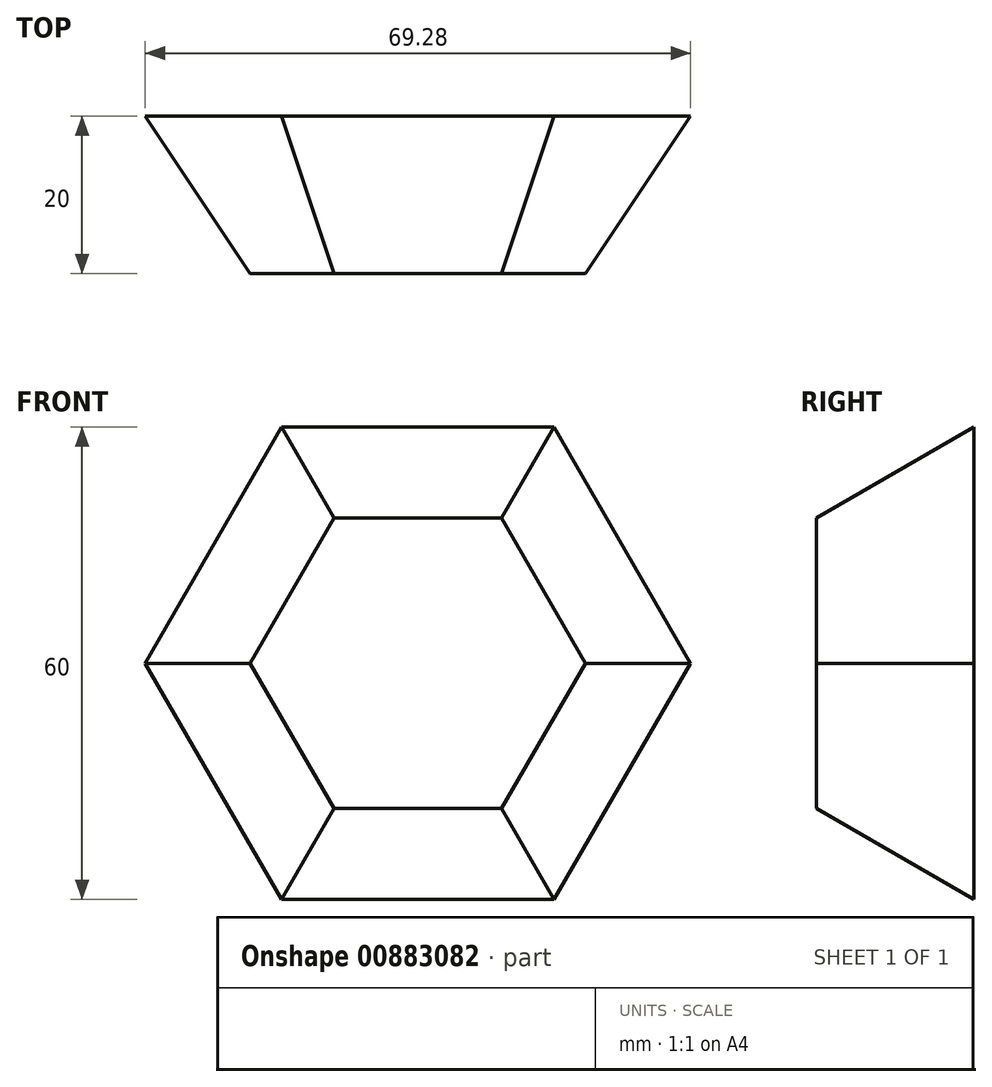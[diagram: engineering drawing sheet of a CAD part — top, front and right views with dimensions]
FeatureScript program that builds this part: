
annotation { "Feature Type Name" : "Feature", "Feature Type Description" : "" }
export const myFeature = defineFeature(function(context is Context, id is Id, definition is map)
    precondition{}
    {
        {
            var Q0;
            Q0=qCreatedBy(makeId("Front.planeOp"),FACE);
            var sketch = newSketch(context, id + "F0", { "sketchPlane" : qUnion([Q0])});
            skCircle(sketch, "E0.cCircle", {"center": v(0, 0) * mm, "radius": 30 * mm, "construction": true});
            skLineSegment(sketch, "E0.0", {"start": v(-17.32, 30) * mm, "end": v(17.32, 30) * mm});
            skLineSegment(sketch, "E0.1", {"start": v(17.32, 30) * mm, "end": v(34.64, 0) * mm});
            skLineSegment(sketch, "E0.2", {"start": v(34.64, 0) * mm, "end": v(17.32, -30) * mm});
            skLineSegment(sketch, "E0.3", {"start": v(17.32, -30) * mm, "end": v(-17.32, -30) * mm});
            skLineSegment(sketch, "E0.4", {"start": v(-17.32, -30) * mm, "end": v(-34.64, 0) * mm});
            skLineSegment(sketch, "E0.5", {"start": v(-34.64, 0) * mm, "end": v(-17.32, 30) * mm});
            skPoint(sketch, "E0.0.midPoint", {"position": v(0, 30) * mm});
            skSolve(sketch);
        }
        {
            var Q0;
            Q0 = qSketchRegion(id + "F0", true);
            extrude(context, id + "F1", {"entities" : qUnion([Q0]), "depth" : 20 * mm, "offsetDistance" : 25 * mm, "hasDraft" : true, "draftAngle" : 30 * degree, "draftPullDirection" : true});
        }
    });
